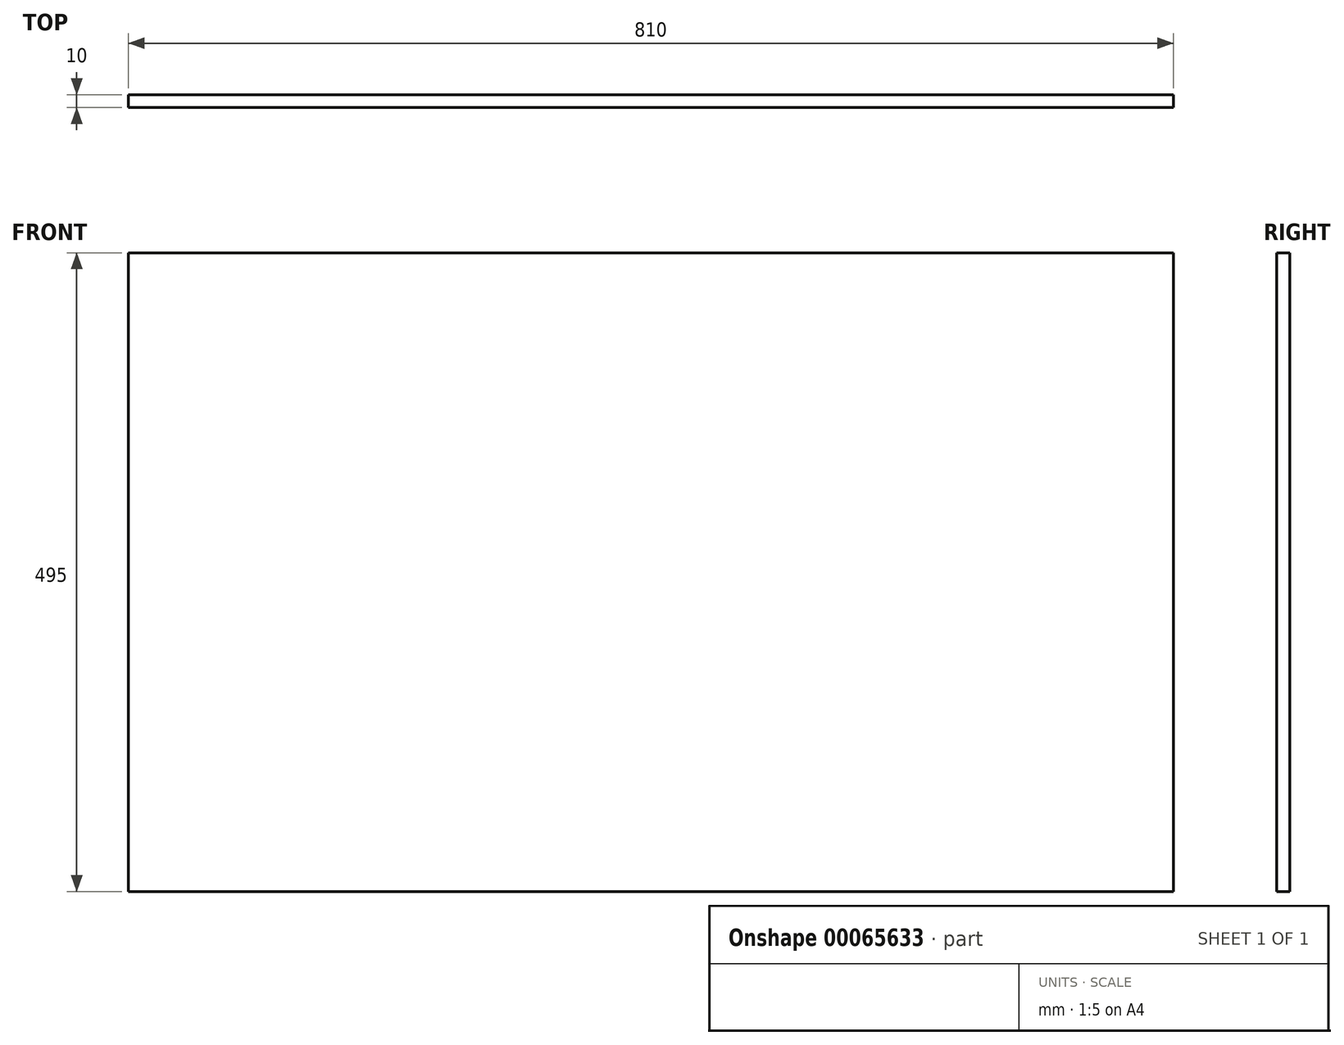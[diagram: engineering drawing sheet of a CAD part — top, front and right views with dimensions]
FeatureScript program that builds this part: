
annotation { "Feature Type Name" : "Feature", "Feature Type Description" : "" }
export const myFeature = defineFeature(function(context is Context, id is Id, definition is map)
    precondition{}
    {
        {
            var Q0;
            Q0=qCreatedBy(makeId("Front.planeOp"),FACE);
            var sketch = newSketch(context, id + "F0", { "sketchPlane" : qUnion([Q0])});
            skLineSegment(sketch, "E0.left", {"start": v(0, 0) * mm, "end": v(0, 495) * mm});
            skLineSegment(sketch, "E1.MirrorCS", {"start": v(810, 0) * mm, "end": v(810, 495) * mm});
            skLineSegment(sketch, "E2", {"start": v(0, 495) * mm, "end": v(810, 495) * mm});
            skLineSegment(sketch, "E3", {"start": v(810, 0) * mm, "end": v(0, 0) * mm});
            skSolve(sketch);
        }
        {
            var Q0;
            Q0 = qSketchRegion(id + "F0", true);
            extrude(context, id + "F1", {"entities" : qUnion([Q0]), "depth" : 10 * mm});
        }
    });
